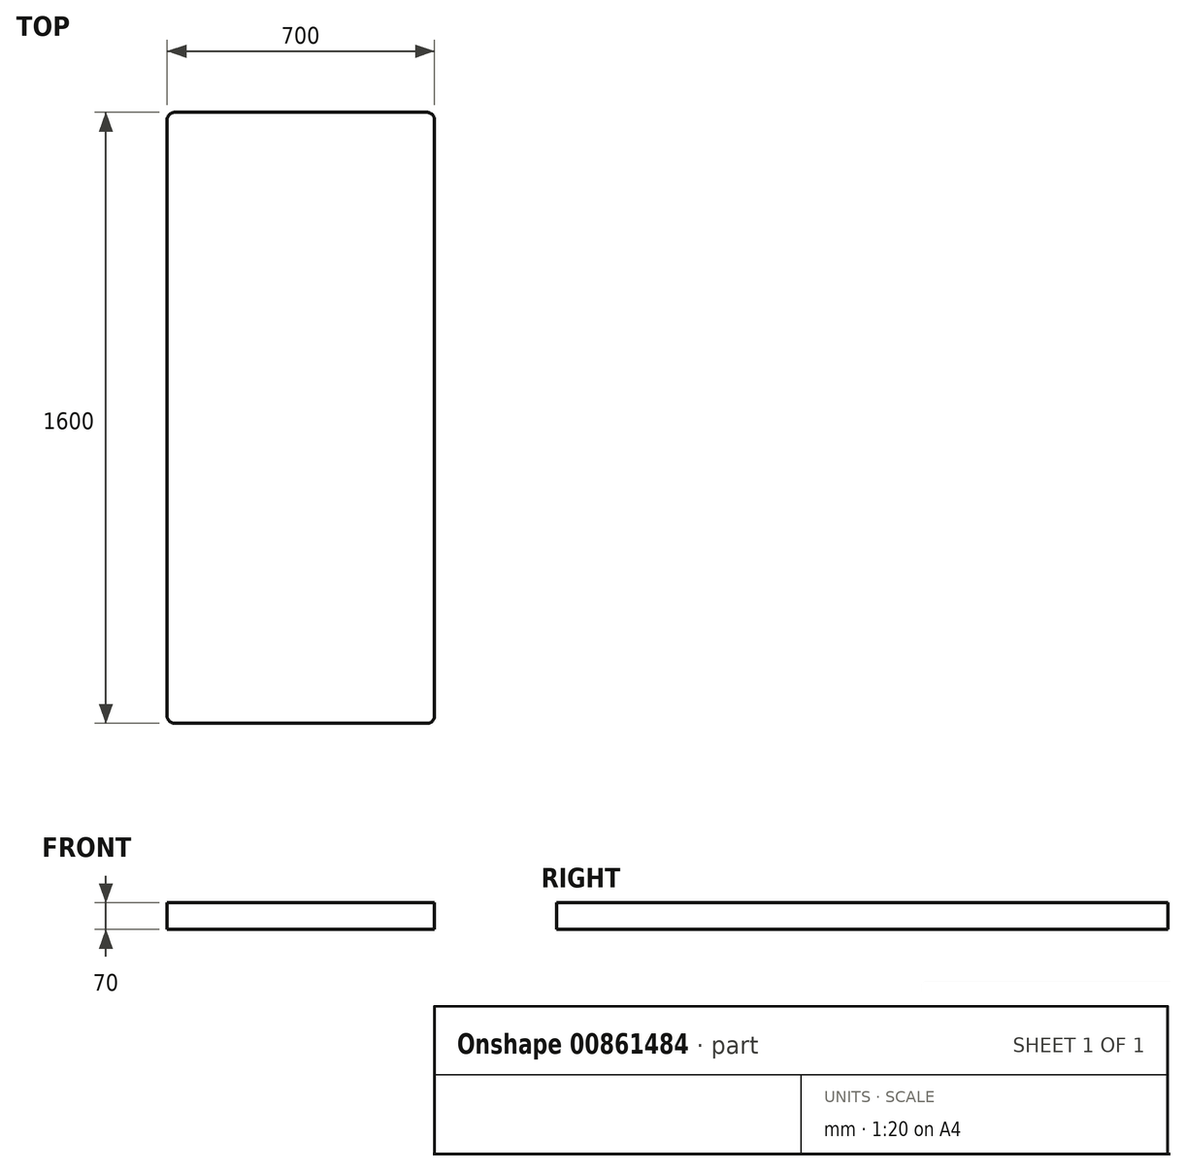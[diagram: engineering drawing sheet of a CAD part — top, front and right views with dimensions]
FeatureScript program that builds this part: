
annotation { "Feature Type Name" : "Feature", "Feature Type Description" : "" }
export const myFeature = defineFeature(function(context is Context, id is Id, definition is map)
    precondition{}
    {
        {
            var Q0;
            Q0=qCreatedBy(makeId("Top.planeOp"),FACE);
            var sketch = newSketch(context, id + "F0", { "sketchPlane" : qUnion([Q0])});
            skLineSegment(sketch, "E0.bottom", {"start": v(330, -800) * mm, "end": v(-330, -800) * mm});
            skLineSegment(sketch, "E0.top", {"start": v(330, 800) * mm, "end": v(-330, 800) * mm});
            skLineSegment(sketch, "E0.left", {"start": v(350, -780) * mm, "end": v(350, 780) * mm});
            skLineSegment(sketch, "E0.right", {"start": v(-350, -780) * mm, "end": v(-350, 780) * mm});
            skPoint(sketch, "E0.middle", {"position": v(0, 0) * mm});
            skPoint(sketch, "E1.visualSharp", {"position": v(-350, -800) * mm});
            skArc(sketch, "E1.filletArc", {"start": v(-350, -780) * mm, "mid": v(-344.14, -794.14) * mm, "end": v(-330, -800) * mm});
            skPoint(sketch, "E2.visualSharp", {"position": v(350, -800) * mm});
            skArc(sketch, "E2.filletArc", {"start": v(330, -800) * mm, "mid": v(344.14, -794.14) * mm, "end": v(350, -780) * mm});
            skPoint(sketch, "E3.visualSharp", {"position": v(350, 800) * mm});
            skArc(sketch, "E3.filletArc", {"start": v(350, 780) * mm, "mid": v(344.14, 794.14) * mm, "end": v(330, 800) * mm});
            skPoint(sketch, "E4.visualSharp", {"position": v(-350, 800) * mm});
            skArc(sketch, "E4.filletArc", {"start": v(-330, 800) * mm, "mid": v(-344.14, 794.14) * mm, "end": v(-350, 780) * mm});
            skSolve(sketch);
        }
        {
            var Q0;
            Q0=makeQuery(id+"F0.imprint","IMPRINT",FACE,{"disambiguationData":[TD([[makeQuery(id+"F0.imprint","IMPRINT",EDGE,{"derivedFrom":sQuery(id+"F0.wireOp",EDGE,"E0.bottom")}),-1.0]])]});
            extrude(context, id + "F1", {"entities" : qUnion([Q0]), "depth" : 70 * mm, "offsetDistance" : 25 * mm});
        }
    });
